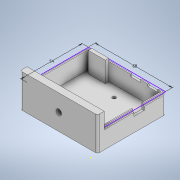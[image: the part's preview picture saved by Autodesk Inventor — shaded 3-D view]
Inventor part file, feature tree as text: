
AUTODESK INVENTOR PART (.ipt)
format: ipt  version: 2022 (Build 260153000, 153)  size: 277,504 bytes
history: native  units: in
note: dims shown in document units (in); Inventor stores cm internally (conversion verified against a paired STEP export)
features: extrude x10, sketch x7, fillet x4
ambient origin geometry x8: Origin, YZ Plane, XZ Plane, XY Plane, X Axis, Y Axis, Z Axis, Center Point
bodies: Solid1 (feature_tree)
feature tree (21):
  sketch  "Sketch1"  dims[d0=2.6772in d2=0.689in d3=0.0in]
  extrude  "Extrusion1"  Depth=0.689in TaperAngle=0.0deg
  extrude  "Extrusion2"  Depth=0.0787in
  extrude  "Extrusion3"  Depth=0.0787in
  extrude  "Extrusion4"  Depth=0.0787in TaperAngle=0.0deg
  extrude  "Extrusion5"  Depth=0.0787in TaperAngle=0.0deg
  extrude  "Extrusion6"  Depth=0.1181in
  extrude  "Extrusion7"  Depth=0.7087in TaperAngle=0.0deg
  extrude  "Extrusion9"  Depth=0.3543in TaperAngle=0.0deg
  fillet  "Fillet7"  Radius=0.0787in
  fillet  "Fillet8"  Radius=0.0394in
  fillet  "Fillet9"  Radius=0.1181in
  fillet  "Fillet11"  Radius=0.2362in
  extrude  "Extrusion10"  Depth=1.1614in TaperAngle=0.0deg
  extrude  "Extrusion11"  Depth=0.3937in
  sketch  "Sketch4"  dims[d5=0.0787in d6=0.0787in]
  sketch  "Sketch7"  dims[d7=0.0787in d11=0.0787in]
  sketch  "Sketch10"  dims[d13=0.6102in d14=0.0in d44=0.0787in d45=0.0in]
  sketch  "Sketch11"  dims[d46=2.6772in d48=0.0787in d49=0.0in]
  sketch  "Sketch16"  dims[d57=0.5906in d58=0.1181in]
  sketch  "Sketch17"  dims[d61=0.5906in d64=0.7087in d65=0.0in d72=0.3543in d73=0.0in d75=0.0787in d76=0.0394in d79=0.1181in d81=0.2362in d82=1.1614in d83=0.0in d85=0.9161in d86=0.8465in d88=0.315in d89=0.1181in d108=0.3543in d109=0.1969in d111=1.0933in d114=0.3937in d115=0.0in d119=0.4528in d120=0.3937in d121=0.0787in d122=0.0787in d123=0.0787in d132=1.9685in d133=2.5197in d135=2.6772in d136=2.126in d138=2.126in d139=0.0394in d140=0.0394in d141=0.0394in d143=2.6772in d144=0.0in d147=0.0787in d148=0.1969in d149=0.2362in d150=0.0in d151=0.3346in d152=0.3346in d153=0.1969in d157=0.0in d158=0.5315in d160=1.126in d161=0.3937in d162=0.0in d40=0.0197in d41=0.0344in d42=0.0197in d43=0.0344in d66=0.0197in d67=0.0344in d84=0.0197in]
